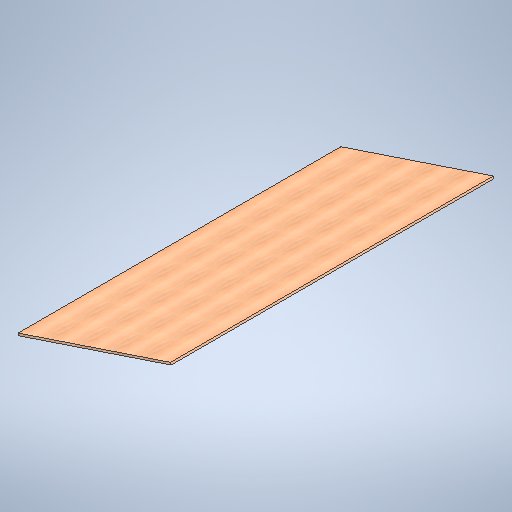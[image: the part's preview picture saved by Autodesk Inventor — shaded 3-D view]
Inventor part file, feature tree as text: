
AUTODESK INVENTOR PART (.ipt)
format: ipt  version: 2025 (Build 290162010, 162A)  size: 303,104 bytes
history: native  units: in
note: dims shown in document units (in); Inventor stores cm internally (conversion verified against a paired STEP export)
features: extrude x1, plane x1, sketch x1
ambient origin geometry x8: Origin, YZ Plane, XZ Plane, XY Plane, X Axis, Y Axis, Z Axis, Center Point
bodies: Body1 (feature_tree)
feature tree (3):
  extrude  "Extrusion2"  Depth=96.0in
  plane  "Work Plane2"
  sketch  "Sketch1"  dims[d5=5.5in d17=3.5in d19=132.0in d23=1.194in d28=1.8188in d33=42.875in d36=0.625in d37=48.0in d38=96.0in d39=0.0in d40=90.0deg]
